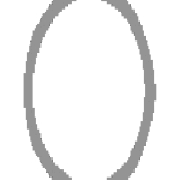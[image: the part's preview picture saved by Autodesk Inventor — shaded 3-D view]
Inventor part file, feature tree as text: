
AUTODESK INVENTOR PART (.ipt)
format: ipt  version: 2021 (Build 250183000, 183)  size: 153,600 bytes
history: native  units: in
note: dims shown in document units (in); Inventor stores cm internally (conversion verified against a paired STEP export)
features: other x5, sketch x2, sweep x1, plane x1
ambient origin geometry x8: Origin, YZ Plane, XZ Plane, XY Plane, X Axis, Y Axis, Z Axis, Center Point
bodies: Solid1 (feature_tree), Body (feature_tree)
feature tree (9):
  other  "Driven Length"
  other  "Frame Generator"
  other  "Start Plane"
  other  "End Plane"
  sweep  "Sweep Path"
  other  "Orientation Work Plane"
  sketch  "Sketch2"  dims[d0=1.0in d1=0.065in]
  plane  "Work Plane3"
  sketch  "Sketch3"  dims[d2=16.5001in d4=-0.0in d5=16.5001in d8=90.0deg d9=16.5001in d10=0.0in d11=0.0in]
